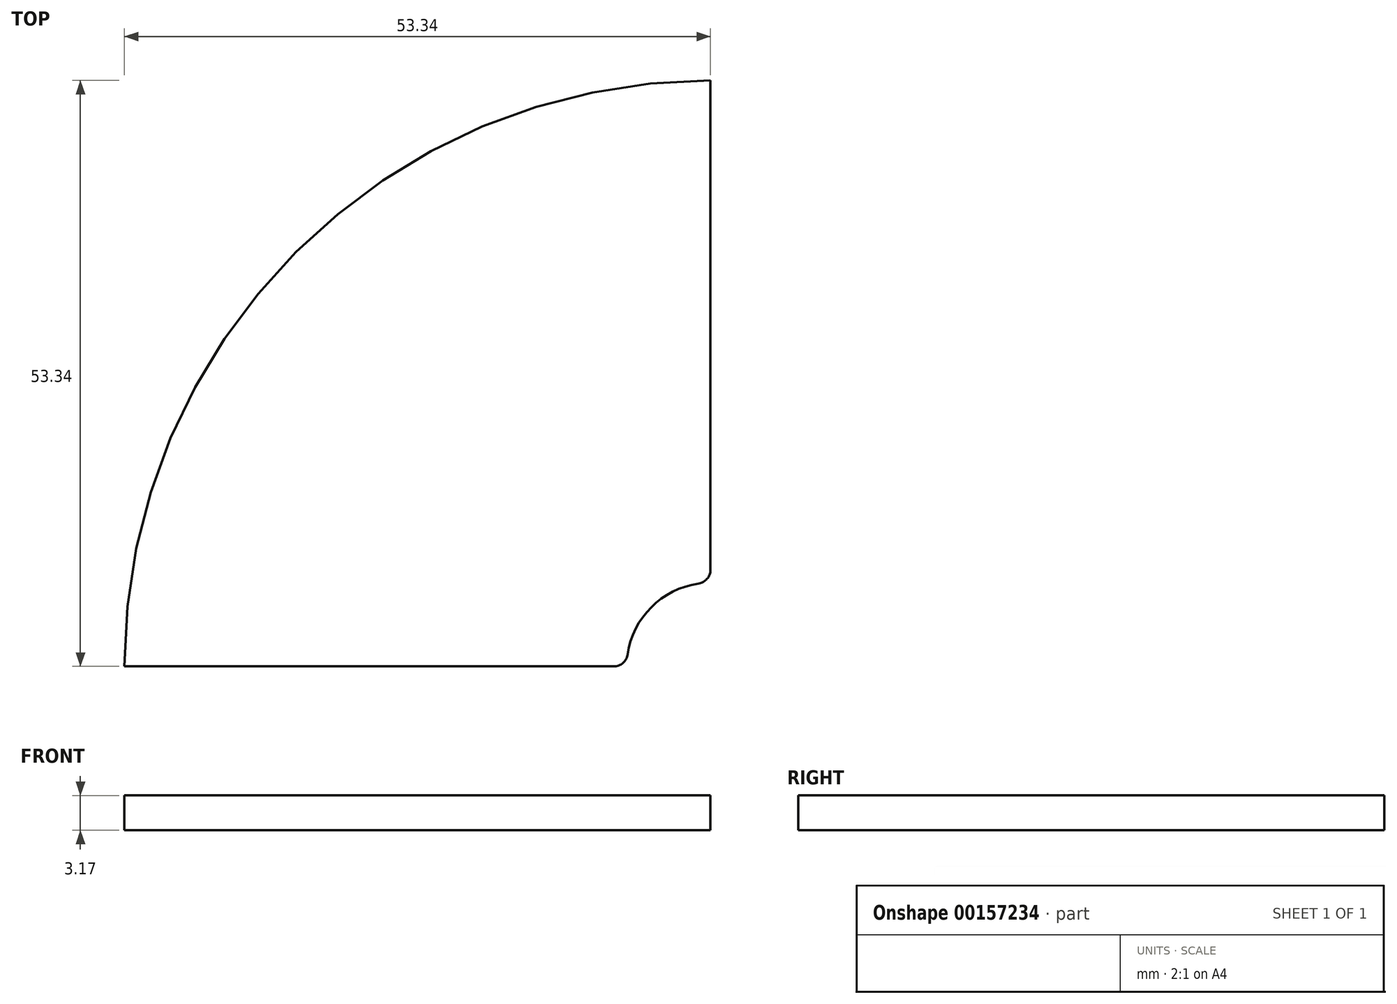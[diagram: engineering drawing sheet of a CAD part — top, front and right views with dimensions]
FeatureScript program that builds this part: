
annotation { "Feature Type Name" : "Feature", "Feature Type Description" : "" }
export const myFeature = defineFeature(function(context is Context, id is Id, definition is map)
    precondition{}
    {
        {
            var Q0;
            Q0=qCreatedBy(makeId("Top.planeOp"),FACE);
            var sketch = newSketch(context, id + "F0", { "sketchPlane" : qUnion([Q0])});
            skArc(sketch, "E0", {"start": v(0, 12.7) * mm, "mid": v(-8.98, 8.98) * mm, "end": v(-12.7, 0) * mm});
            skArc(sketch, "E1", {"start": v(0, 7.62) * mm, "mid": v(-5.39, 5.39) * mm, "end": v(-7.62, 0) * mm});
            skLineSegment(sketch, "E2", {"start": v(0, 48.26) * mm, "end": v(0, 7.62) * mm});
            skLineSegment(sketch, "E3", {"start": v(-7.62, 0) * mm, "end": v(-48.26, 0) * mm});
            skLineSegment(sketch, "E4", {"start": v(0, 48.26) * mm, "end": v(0, 53.34) * mm});
            skArc(sketch, "E5", {"start": v(0, 53.34) * mm, "mid": v(-37.72, 37.72) * mm, "end": v(-53.34, 0) * mm});
            skArc(sketch, "E6", {"start": v(0, 48.26) * mm, "mid": v(-34.12, 34.12) * mm, "end": v(-48.26, 0) * mm});
            skLineSegment(sketch, "E7", {"start": v(-48.26, 0) * mm, "end": v(-53.34, 0) * mm});
            skSolve(sketch);
        }
        {
            var Q0;
            Q0 = qSketchRegion(id + "F0", true);
            extrude(context, id + "F1", {"entities" : qUnion([Q0]), "depth" : 3.17 * mm});
        }
        {
            var Q0;
            Q0=makeQuery(id+"F1.opExtrude","SWEPT_EDGE",EDGE,{"disambiguationData":[OSD([sQuery(id+"F0.wireOp",EDGE,"E3"),sQuery(id+"F0.wireOp",EDGE,"h6lfakL9-NsbF-VXKI-ImJH-NQLVMbCS3c2D")])]});
            var Q1;
            Q1=makeQuery(id+"F1.opExtrude","SWEPT_EDGE",EDGE,{"disambiguationData":[OSD([sQuery(id+"F0.wireOp",EDGE,"E3"),sQuery(id+"F0.wireOp",EDGE,"qGbQAuce-huhQ-BNAD-3zQz-poU3iRitGAEc")])]});
            var Q2;
            Q2=makeQuery(id+"F1.opExtrude","SWEPT_EDGE",EDGE,{"disambiguationData":[OSD([sQuery(id+"F0.wireOp",EDGE,"qGbQAuce-huhQ-BNAD-3zQz-poU3iRitGAEc"),sQuery(id+"F0.wireOp",EDGE,"db0AO0WG-tgtI-ao0p-V3zy-WFwqwsmLqmrI")])]});
            var Q3;
            Q3=makeQuery(id+"F1.opExtrude","SWEPT_EDGE",EDGE,{"disambiguationData":[OSD([sQuery(id+"F0.wireOp",EDGE,"db0AO0WG-tgtI-ao0p-V3zy-WFwqwsmLqmrI"),sQuery(id+"F0.wireOp",EDGE,"pvZunOkA-7jXq-BQh8-ski9-8k4NY9AG8ory")])]});
            var Q4;
            Q4=makeQuery(id+"F1.opExtrude","SWEPT_EDGE",EDGE,{"disambiguationData":[OSD([sQuery(id+"F0.wireOp",EDGE,"EKPPo4To-sp4V-JdMd-LWjO-mS29bPzMoleU"),sQuery(id+"F0.wireOp",EDGE,"idsOBNKc-UxlU-6TvL-qgJw-oBkyVF1Ez4kc")])]});
            var Q5;
            Q5=makeQuery(id+"F1.opExtrude","SWEPT_EDGE",EDGE,{"disambiguationData":[OSD([sQuery(id+"F0.wireOp",EDGE,"HvcRj3k9-Tqxx-2YjV-fosB-yp6NyYda0rG6"),sQuery(id+"F0.wireOp",EDGE,"sVnGrA0B-yfB9-gLhw-ne8e-MgMp0sl9ulvc")])]});
            var Q6;
            Q6=makeQuery(id+"F1.opExtrude","SWEPT_EDGE",EDGE,{"disambiguationData":[OSD([sQuery(id+"F0.wireOp",EDGE,"sVnGrA0B-yfB9-gLhw-ne8e-MgMp0sl9ulvc"),sQuery(id+"F0.wireOp",EDGE,"mOZbsW1C-BQO2-IUwa-Z2G7-xaAvLpF8PRqF")])]});
            var Q7;
            Q7=makeQuery(id+"F1.opExtrude","SWEPT_EDGE",EDGE,{"disambiguationData":[OSD([sQuery(id+"F0.wireOp",EDGE,"2YQRd3qW-rXrK-ETWW-qxw0-uIeebvumD2Ge"),sQuery(id+"F0.wireOp",EDGE,"EKPPo4To-sp4V-JdMd-LWjO-mS29bPzMoleU")])]});
            var Q8;
            Q8=makeQuery(id+"F1.opExtrude","SWEPT_EDGE",EDGE,{"disambiguationData":[OSD([sQuery(id+"F0.wireOp",EDGE,"E2"),sQuery(id+"F0.wireOp",EDGE,"HvcRj3k9-Tqxx-2YjV-fosB-yp6NyYda0rG6")])]});
            var Q9;
            Q9=makeQuery(id+"F1.opExtrude","SWEPT_EDGE",EDGE,{"disambiguationData":[OSD([sQuery(id+"F0.wireOp",EDGE,"E2"),sQuery(id+"F0.wireOp",EDGE,"2YQRd3qW-rXrK-ETWW-qxw0-uIeebvumD2Ge")])]});
            var Q10;
            Q10=makeQuery(id+"F1.opExtrude","SWEPT_EDGE",EDGE,{"disambiguationData":[OSD([sQuery(id+"F0.wireOp",EDGE,"xOcS55fQ-7izb-S3VQ-fFKU-ku18nXWC37Vr"),sQuery(id+"F0.wireOp",EDGE,"Gnfei352-cxUN-oDTe-TOQm-WI0Q7B94aKId")])]});
            var Q11;
            Q11=makeQuery(id+"F1.opExtrude","SWEPT_EDGE",EDGE,{"disambiguationData":[OSD([sQuery(id+"F0.wireOp",EDGE,"Gnfei352-cxUN-oDTe-TOQm-WI0Q7B94aKId"),sQuery(id+"F0.wireOp",EDGE,"h6lfakL9-NsbF-VXKI-ImJH-NQLVMbCS3c2D")])]});
            fillet(context, id + "F2", {"entities" : qUnion([Q0, Q1, Q2, Q3, Q4, Q5, Q6, Q7, Q8, Q9, Q10, Q11]), "radius" : 1.27 * mm, "tangentPropagation" : true, "allowEdgeOverflow" : false});
        }
    });
